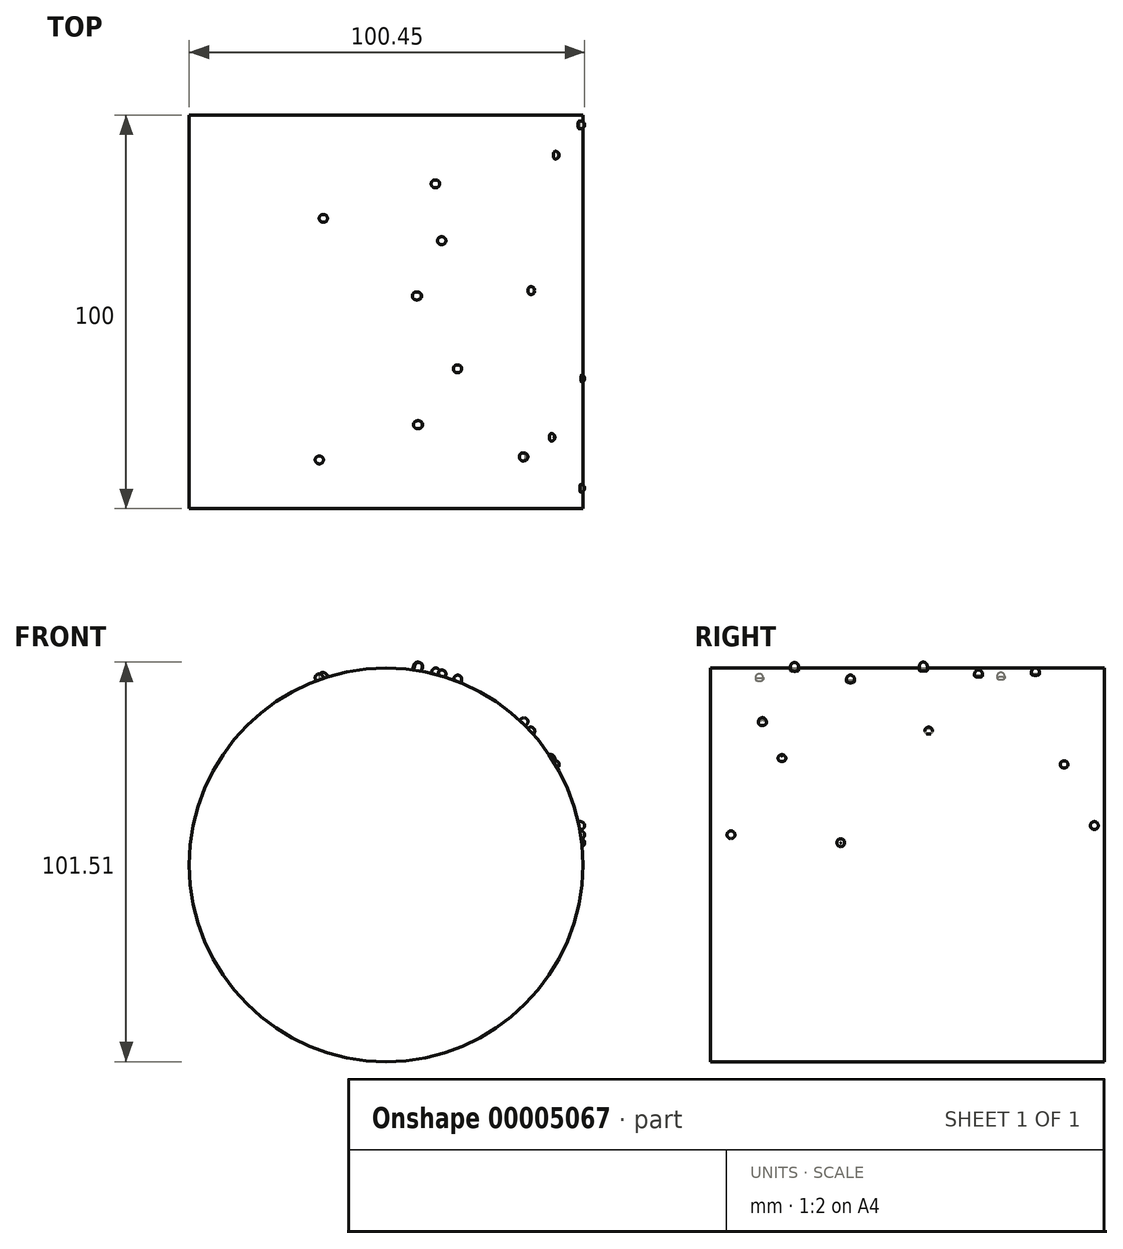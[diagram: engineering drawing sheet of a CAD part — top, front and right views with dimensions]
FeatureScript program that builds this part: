
annotation { "Feature Type Name" : "Feature", "Feature Type Description" : "" }
export const myFeature = defineFeature(function(context is Context, id is Id, definition is map)
    precondition{}
    {
        {
            var Q0;
            Q0=qCreatedBy(makeId("Front.planeOp"),FACE);
            var sketch = newSketch(context, id + "F0", { "sketchPlane" : qUnion([Q0])});
            skCircle(sketch, "E0.cCircle", {"center": v(0, 0) * mm, "radius": 45 * mm, "construction": true});
            skLineSegment(sketch, "E0.0", {"start": v(45, 14.62) * mm, "end": v(45, -14.62) * mm});
            skLineSegment(sketch, "E0.1", {"start": v(45, -14.62) * mm, "end": v(27.81, -38.28) * mm});
            skLineSegment(sketch, "E0.2", {"start": v(27.81, -38.28) * mm, "end": v(0, -47.32) * mm});
            skLineSegment(sketch, "E0.3", {"start": v(0, -47.32) * mm, "end": v(-27.81, -38.28) * mm});
            skLineSegment(sketch, "E0.4", {"start": v(-27.81, -38.28) * mm, "end": v(-45, -14.62) * mm});
            skLineSegment(sketch, "E0.5", {"start": v(-45, -14.62) * mm, "end": v(-45, 14.62) * mm});
            skLineSegment(sketch, "E0.6", {"start": v(-45, 14.62) * mm, "end": v(-27.81, 38.28) * mm});
            skLineSegment(sketch, "E0.7", {"start": v(-27.81, 38.28) * mm, "end": v(0, 47.32) * mm});
            skLineSegment(sketch, "E0.8", {"start": v(0, 47.32) * mm, "end": v(27.81, 38.28) * mm});
            skLineSegment(sketch, "E0.9", {"start": v(27.81, 38.28) * mm, "end": v(45, 14.62) * mm});
            skPoint(sketch, "E0.0.midPoint", {"position": v(45, 0) * mm});
            skSolve(sketch);
        }
        {
            var Q0;
            Q0=qSketchRegion(id+"F0",true);
            extrude(context, id + "F1", {"entities" : qUnion([Q0]), "depth" : 100 * mm, "symmetric" : true});
        }
        {
            var Q0;
            Q0=makeQuery(id+"F1.opExtrude","SWEPT_FACE",FACE,{"disambiguationData":[OSD([sQuery(id+"F0.wireOp",EDGE,"E0.8")])]});
            var sketch = newSketch(context, id + "F2", { "sketchPlane" : qUnion([Q0])});
            skCircle(sketch, "E1", {"center": v(-6.21, -28.67) * mm, "radius": 1 * mm});
            skCircle(sketch, "E2", {"center": v(4.22, -14.46) * mm, "radius": 1 * mm});
            skCircle(sketch, "E3", {"center": v(-6.5, 4.05) * mm, "radius": 1 * mm});
            skCircle(sketch, "E4", {"center": v(0, 18.08) * mm, "radius": 1 * mm});
            skCircle(sketch, "E5", {"center": v(-1.66, 32.53) * mm, "radius": 1 * mm});
            skSolve(sketch);
        }
        {
            var Q0;
            Q0=qSketchRegion(id+"F2",true);
            extrude(context, id + "F3", {"entities" : qUnion([Q0]), "operationType" : NewBodyOperationType.ADD, "depth" : 7 * mm});
        }
        {
            var Q0;
            Q0=makeQuery(id+"F1.opExtrude","SWEPT_FACE",FACE,{"disambiguationData":[OSD([sQuery(id+"F0.wireOp",EDGE,"E0.9")])]});
            var sketch = newSketch(context, id + "F4", { "sketchPlane" : qUnion([Q0])});
            skCircle(sketch, "E6", {"center": v(-36.85, 7.93) * mm, "radius": 1 * mm});
            skCircle(sketch, "E7", {"center": v(-31.88, -3.7) * mm, "radius": 1 * mm});
            skCircle(sketch, "E8", {"center": v(5.4, 4.97) * mm, "radius": 1 * mm});
            skCircle(sketch, "E9", {"center": v(39.8, -5.58) * mm, "radius": 1 * mm});
            skSolve(sketch);
        }
        {
            var Q0;
            Q0=qSketchRegion(id+"F4",true);
            extrude(context, id + "F5", {"entities" : qUnion([Q0]), "operationType" : NewBodyOperationType.ADD, "depth" : 7 * mm});
        }
        {
            var Q0;
            Q0=makeQuery(id+"F1.opExtrude","SWEPT_FACE",FACE,{"disambiguationData":[OSD([sQuery(id+"F0.wireOp",EDGE,"E0.7")])]});
            var sketch = newSketch(context, id + "F6", { "sketchPlane" : qUnion([Q0])});
            skCircle(sketch, "E10", {"center": v(1.06, 23.76) * mm, "radius": 1 * mm});
            skCircle(sketch, "E11", {"center": v(0, -37.62) * mm, "radius": 1 * mm});
            skSolve(sketch);
        }
        {
            var Q0;
            Q0=qSketchRegion(id+"F6",true);
            extrude(context, id + "F7", {"entities" : qUnion([Q0]), "operationType" : NewBodyOperationType.ADD, "depth" : 6 * mm});
        }
        {
            var Q0;
            Q0=makeQuery(id+"F1.opExtrude","SWEPT_FACE",FACE,{"disambiguationData":[OSD([sQuery(id+"F0.wireOp",EDGE,"E0.0")])]});
            var sketch = newSketch(context, id + "F8", { "sketchPlane" : qUnion([Q0])});
            skCircle(sketch, "E12", {"center": v(-16.94, 5.62) * mm, "radius": 1 * mm});
            skCircle(sketch, "E13", {"center": v(47.5, 9.98) * mm, "radius": 1 * mm});
            skCircle(sketch, "E14", {"center": v(-44.82, 7.65) * mm, "radius": 1 * mm});
            skSolve(sketch);
        }
        {
            var Q0;
            Q0=qSketchRegion(id+"F8",true);
            extrude(context, id + "F9", {"entities" : qUnion([Q0]), "operationType" : NewBodyOperationType.ADD, "depth" : 7 * mm});
        }
        {
            var Q0;
            Q0=qCreatedBy(makeId("Front.planeOp"),FACE);
            var sketch = newSketch(context, id + "F10", { "sketchPlane" : qUnion([Q0])});
            skCircle(sketch, "E15", {"center": v(1.55, 0) * mm, "radius": 50 * mm});
            skSolve(sketch);
        }
        {
            var Q0;
            Q0=qSketchRegion(id+"F10",true);
            extrude(context, id + "F11", {"entities" : qUnion([Q0]), "operationType" : NewBodyOperationType.ADD, "depth" : 100 * mm, "symmetric" : true});
        }
        {
            var Q0;
            Q0=makeQuery(id+"F7.opExtrude","CAP_EDGE",EDGE,{"disambiguationData":[OSD([sQuery(id+"F6.wireOp",EDGE,"E11")])],"isStart":false});
            var Q1;
            Q1=makeQuery(id+"F7.opExtrude","CAP_EDGE",EDGE,{"disambiguationData":[OSD([sQuery(id+"F6.wireOp",EDGE,"E10")])],"isStart":false});
            var Q2;
            Q2=makeQuery(id+"F3.opExtrude","CAP_EDGE",EDGE,{"disambiguationData":[OSD([sQuery(id+"F2.wireOp",EDGE,"E5")])],"isStart":false});
            var Q3;
            Q3=makeQuery(id+"F3.opExtrude","CAP_EDGE",EDGE,{"disambiguationData":[OSD([sQuery(id+"F2.wireOp",EDGE,"E4")])],"isStart":false});
            var Q4;
            Q4=makeQuery(id+"F3.opExtrude","CAP_EDGE",EDGE,{"disambiguationData":[OSD([sQuery(id+"F2.wireOp",EDGE,"E3")])],"isStart":false});
            var Q5;
            Q5=makeQuery(id+"F3.opExtrude","CAP_EDGE",EDGE,{"disambiguationData":[OSD([sQuery(id+"F2.wireOp",EDGE,"E2")])],"isStart":false});
            var Q6;
            Q6=makeQuery(id+"F3.opExtrude","CAP_EDGE",EDGE,{"disambiguationData":[OSD([sQuery(id+"F2.wireOp",EDGE,"E1")])],"isStart":false});
            var Q7;
            Q7=makeQuery(id+"F5.opExtrude","CAP_EDGE",EDGE,{"disambiguationData":[OSD([sQuery(id+"F4.wireOp",EDGE,"E6")])],"isStart":false});
            var Q8;
            Q8=makeQuery(id+"F5.opExtrude","CAP_EDGE",EDGE,{"disambiguationData":[OSD([sQuery(id+"F4.wireOp",EDGE,"E8")])],"isStart":false});
            var Q9;
            Q9=makeQuery(id+"F5.opExtrude","CAP_EDGE",EDGE,{"disambiguationData":[OSD([sQuery(id+"F4.wireOp",EDGE,"E9")])],"isStart":false});
            var Q10;
            Q10=makeQuery(id+"F5.opExtrude","CAP_EDGE",EDGE,{"disambiguationData":[OSD([sQuery(id+"F4.wireOp",EDGE,"E7")])],"isStart":false});
            var Q11;
            Q11=makeQuery(id+"F9.opExtrude","CAP_EDGE",EDGE,{"disambiguationData":[OSD([sQuery(id+"F8.wireOp",EDGE,"E14")])],"isStart":false});
            var Q12;
            Q12=makeQuery(id+"F9.opExtrude","CAP_EDGE",EDGE,{"disambiguationData":[OSD([sQuery(id+"F8.wireOp",EDGE,"E12")])],"isStart":false});
            var Q13;
            Q13=makeQuery(id+"F9.opExtrude","CAP_EDGE",EDGE,{"disambiguationData":[OSD([sQuery(id+"F8.wireOp",EDGE,"E13")])],"isStart":false});
            fillet(context, id + "F12", {"entities" : qUnion([Q0, Q1, Q2, Q3, Q4, Q5, Q6, Q7, Q8, Q9, Q10, Q11, Q12, Q13]), "radius" : 1 * mm, "tangentPropagation" : true, "allowEdgeOverflow" : false});
        }
    });
